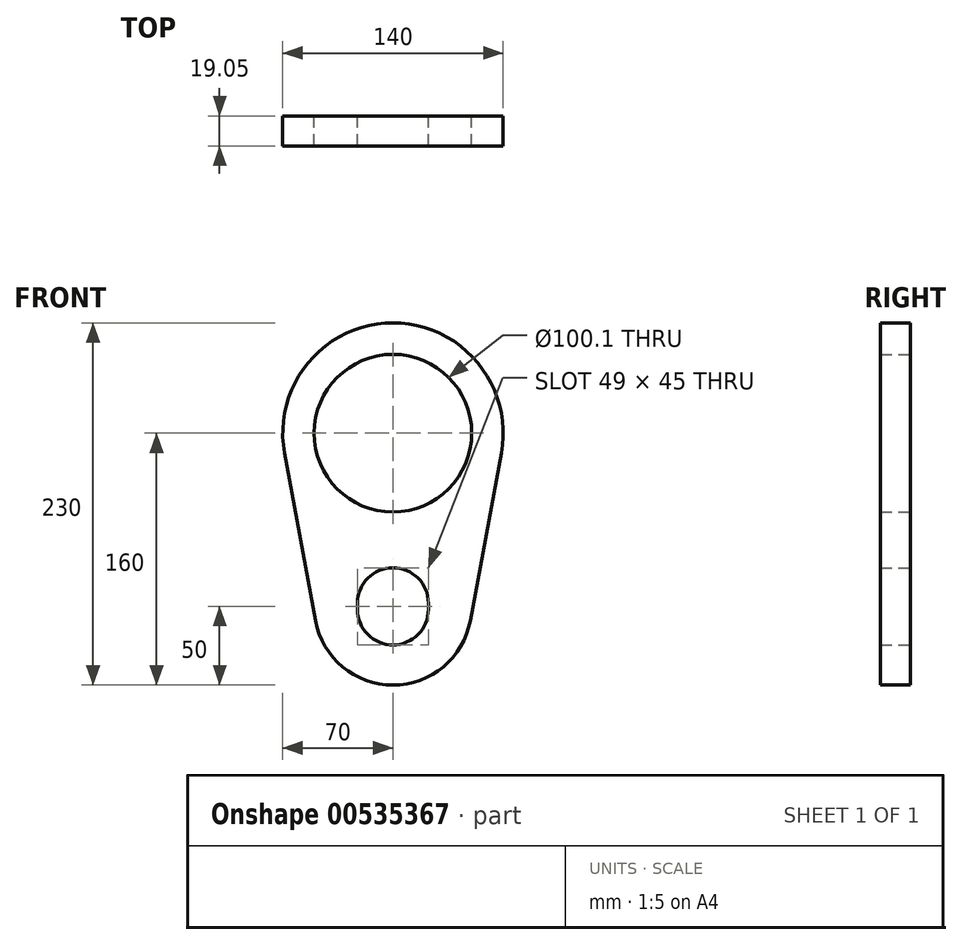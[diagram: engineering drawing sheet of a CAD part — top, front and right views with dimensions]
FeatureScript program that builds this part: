
annotation { "Feature Type Name" : "Feature", "Feature Type Description" : "" }
export const myFeature = defineFeature(function(context is Context, id is Id, definition is map)
    precondition{}
    {
        {
            var Q0;
            Q0=qCreatedBy(makeId("Front.planeOp"),FACE);
            var sketch = newSketch(context, id + "F0", { "sketchPlane" : qUnion([Q0])});
            skArc(sketch, "E0", {"start": v(68.83, -12.73) * mm, "mid": v(0, 70) * mm, "end": v(-68.83, -12.73) * mm});
            skLineSegment(sketch, "E1", {"start": v(-68.83, -12.73) * mm, "end": v(-49.17, -119.1) * mm});
            skLineSegment(sketch, "E2", {"start": v(0, 0) * mm, "end": v(0, -110) * mm, "construction": true});
            skLineSegment(sketch, "E3.MirrorCS", {"start": v(68.83, -12.73) * mm, "end": v(49.17, -119.1) * mm});
            skArc(sketch, "E4.trimOffspring", {"start": v(-49.17, -119.1) * mm, "mid": v(0, -160) * mm, "end": v(49.17, -119.1) * mm});
            skCircle(sketch, "E5", {"center": v(0, 0) * mm, "radius": 50.05 * mm});
            skLineSegment(sketch, "E6", {"start": v(0, -108) * mm, "end": v(0, -112) * mm});
            skArc(sketch, "E7.0.startCap", {"start": v(-22.5, -108) * mm, "mid": v(0, -85.5) * mm, "end": v(22.5, -108) * mm});
            skArc(sketch, "E7.0.endCap", {"start": v(22.5, -112) * mm, "mid": v(0, -134.5) * mm, "end": v(-22.5, -112) * mm});
            skLineSegment(sketch, "E7.0.left", {"start": v(22.5, -108) * mm, "end": v(22.5, -112) * mm});
            skLineSegment(sketch, "E7.0.right", {"start": v(-22.5, -108) * mm, "end": v(-22.5, -112) * mm});
            skSolve(sketch);
        }
        {
            var Q0;
            Q0=qSketchRegion(id+"F0",true);
            extrude(context, id + "F1", {"entities" : qUnion([Q0]), "depth" : 19.05 * mm, "offsetDistance" : 25.4 * mm});
        }
    });
